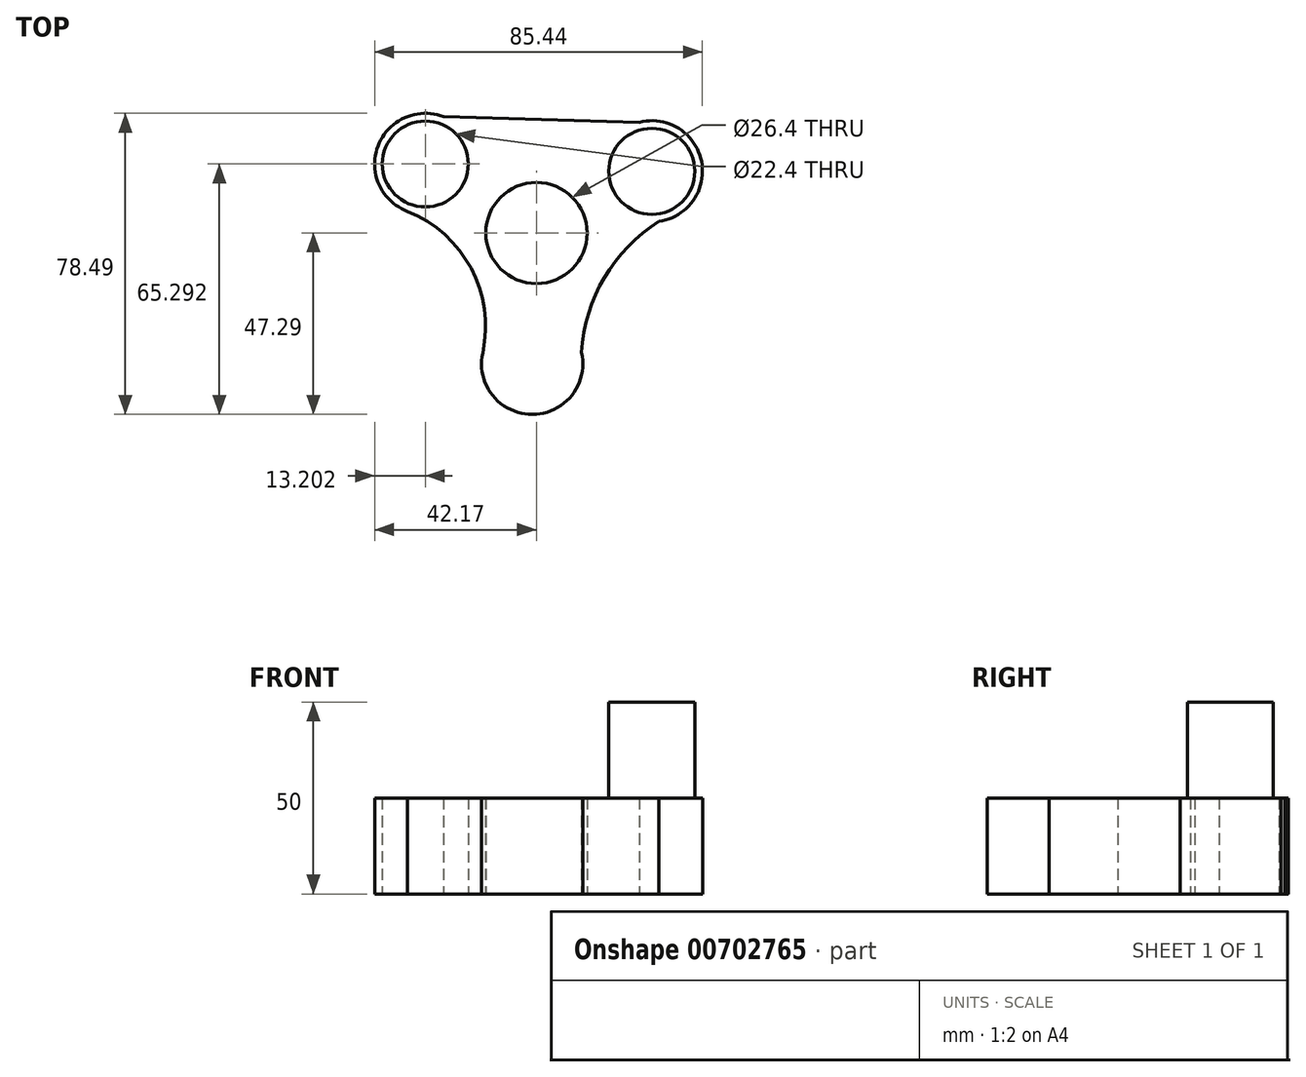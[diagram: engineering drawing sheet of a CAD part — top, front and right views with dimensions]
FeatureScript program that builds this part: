
annotation { "Feature Type Name" : "Feature", "Feature Type Description" : "" }
export const myFeature = defineFeature(function(context is Context, id is Id, definition is map)
    precondition{}
    {
        {
            var Q0;
            Q0=qCreatedBy(makeId("Top.planeOp"),FACE);
            var sketch = newSketch(context, id + "F0", { "sketchPlane" : qUnion([Q0])});
            skCircle(sketch, "E0", {"center": v(0, 0) * mm, "radius": 11.2 * mm});
            skCircle(sketch, "E1", {"center": v(0, 0) * mm, "radius": 13.2 * mm});
            skCircle(sketch, "E2", {"center": v(-28.97, 18) * mm, "radius": 11.2 * mm});
            skArc(sketch, "E3", {"start": v(-24.21, 30.32) * mm, "mid": v(-41.3, 22.7) * mm, "end": v(-33.6, 5.64) * mm});
            skCircle(sketch, "E4.1.0", {"center": v(-1.1, -34.09) * mm, "radius": 13.2 * mm});
            skCircle(sketch, "E4.2.0", {"center": v(30.07, 16.09) * mm, "radius": 13.2 * mm});
            skLineSegment(sketch, "E5", {"start": v(-24.21, 30.32) * mm, "end": v(26.83, 28.88) * mm});
            skArc(sketch, "E6", {"start": v(-14, -31.22) * mm, "mid": v(-17.14, -9.02) * mm, "end": v(-33.97, 5.79) * mm});
            skArc(sketch, "E7", {"start": v(31.9, 3.01) * mm, "mid": v(17.7, -11.62) * mm, "end": v(11.76, -31.13) * mm});
            skSolve(sketch);
        }
        {
            var Q0;
            Q0 = qSketchRegion(id + "F0", true);
            extrude(context, id + "F1", {"entities" : qUnion([Q0]), "depth" : 25 * mm, "offsetDistance" : 25 * mm});
        }
        {
            var Q0;
            Q0=makeQuery(id+"F1.opExtrude","CAP_FACE",FACE,{"disambiguationData":[OSD([sQuery(id+"F0.wireOp",EDGE,"E1"),sQuery(id+"F0.wireOp",EDGE,"E2"),sQuery(id+"F0.wireOp",EDGE,"E3"),sQuery(id+"F0.wireOp",EDGE,"E4.1.0"),sQuery(id+"F0.wireOp",EDGE,"E4.2.0"),sQuery(id+"F0.wireOp",EDGE,"E5"),sQuery(id+"F0.wireOp",EDGE,"E6"),sQuery(id+"F0.wireOp",EDGE,"E7")])],"isStart":false});
            var sketch = newSketch(context, id + "F2", { "sketchPlane" : qUnion([Q0])});
            skCircle(sketch, "E8", {"center": v(30.07, 16.09) * mm, "radius": 11.2 * mm});
            skSolve(sketch);
        }
        {
            var Q0;
            Q0 = qSketchRegion(id + "F2", true);
            extrude(context, id + "F3", {"entities" : qUnion([Q0]), "operationType" : NewBodyOperationType.ADD, "depth" : 25 * mm, "offsetDistance" : 25 * mm});
        }
    });
